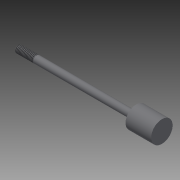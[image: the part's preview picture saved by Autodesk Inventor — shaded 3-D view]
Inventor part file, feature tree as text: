
AUTODESK INVENTOR PART (.ipt)
format: ipt  version: 2014 (Build 180170000, 170)  size: 131,584 bytes
history: native  units: in
note: dims shown in document units (in); Inventor stores cm internally (conversion verified against a paired STEP export)
features: other x49, revolve x3, sketch x3, thread x1
ambient origin geometry x8: Origin, YZ Plane, XZ Plane, XY Plane, X Axis, Y Axis, Z Axis, Center Point
bodies: Solid1 (feature_tree)
feature tree (56):
  revolve  "Revolution1"  [1 undecoded]
  thread  "Thread1"  [1 undecoded]
  revolve  "Revolution2"  [1 undecoded]
  revolve  "Revolution3"  [1 undecoded]
  other  "h1_XY"
  other  "h1_YZ"
  other  "h1_ZX"
  other  "h1_X"
  other  "h1_Y"
  other  "h1_Z"
  other  "h1_Center"
  other  "h2_XY"
  other  "h2_YZ"
  other  "h2_ZX"
  other  "h2_X"
  other  "h2_Y"
  other  "h2_Z"
  other  "h2_Center"
  other  "k1_XY"
  other  "k1_YZ"
  other  "k1_ZX"
  other  "k1_X"
  other  "k1_Y"
  other  "k1_Z"
  other  "k1_Center"
  other  "k2_XY"
  other  "k2_YZ"
  other  "k2_ZX"
  other  "k2_X"
  other  "k2_Y"
  other  "k2_Z"
  other  "k2_Center"
  other  "start_XY"
  other  "start_YZ"
  other  "start_ZX"
  other  "start_X"
  other  "start_Y"
  other  "start_Z"
  other  "start_Center"
  other  "to_prc_XY"
  other  "to_prc_YZ"
  other  "to_prc_ZX"
  other  "to_prc_X"
  other  "to_prc_Y"
  other  "to_prc_Z"
  other  "to_prc_Center"
  other  "to_rod_guide_XY"
  other  "to_rod_guide_YZ"
  other  "to_rod_guide_ZX"
  other  "to_rod_guide_X"
  other  "to_rod_guide_Y"
  other  "to_rod_guide_Z"
  other  "to_rod_guide_Center"
  sketch  "Sketch_3"  dims[d0=360.0deg d1=0.49in d2=3.291in d3=360.0deg]
  sketch  "Sketch_17"
  sketch  "Sketch_12"  dims[d4=360.0deg]
note: 4 required parameter values undecoded (feature->parameter linkage not recoverable at this tier; creation-order binding heuristic only, values carry confidence <= 0.55)